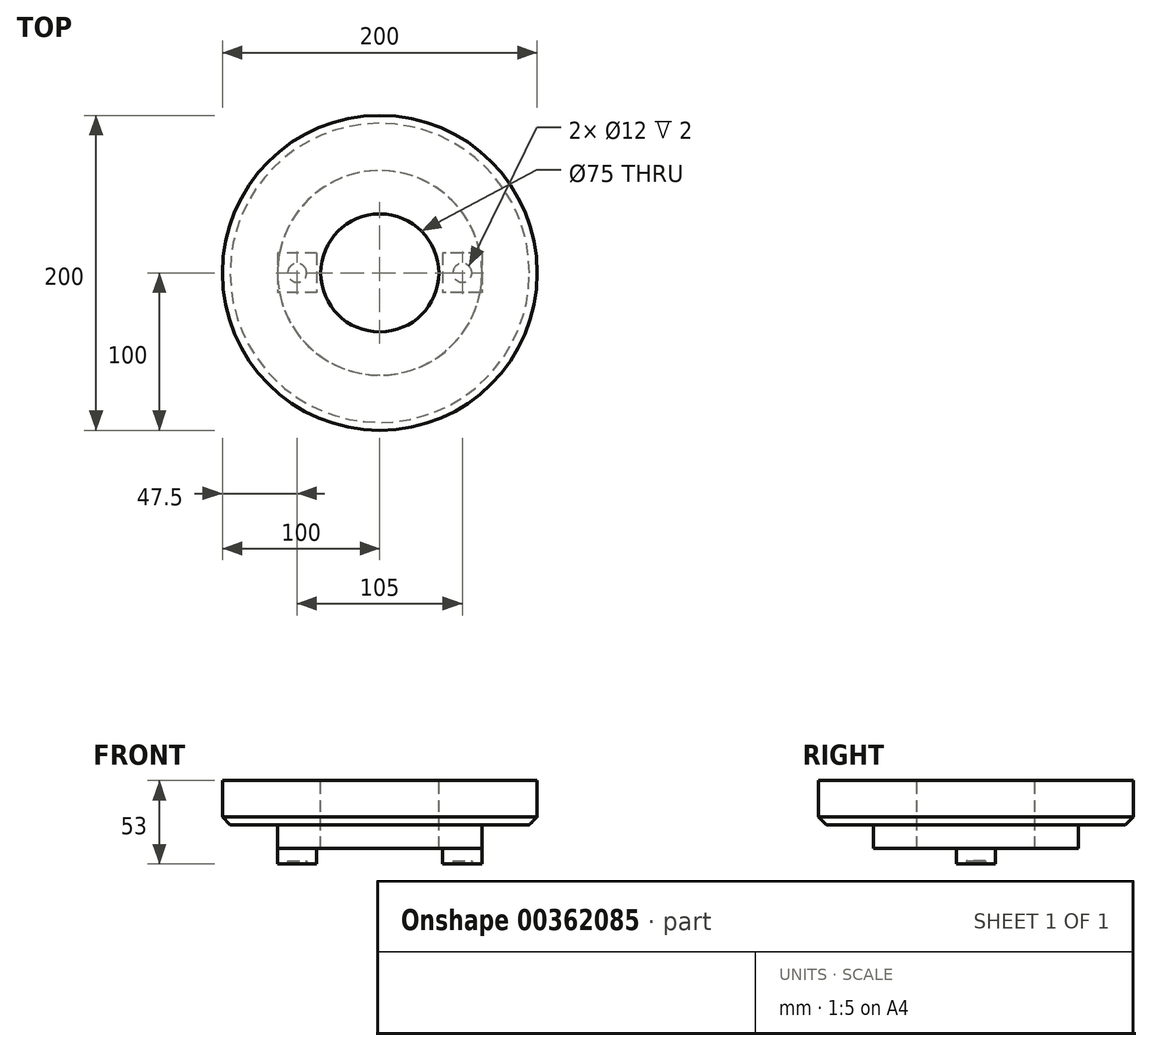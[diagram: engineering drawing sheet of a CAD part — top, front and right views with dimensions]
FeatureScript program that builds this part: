
annotation { "Feature Type Name" : "Feature", "Feature Type Description" : "" }
export const myFeature = defineFeature(function(context is Context, id is Id, definition is map)
    precondition{}
    {
        {
            var Q0;
            Q0=qCreatedBy(makeId("Top.planeOp"),FACE);
            var sketch = newSketch(context, id + "F0", { "sketchPlane" : qUnion([Q0])});
            skCircle(sketch, "E0", {"center": v(0, 0) * mm, "radius": 100 * mm});
            skSolve(sketch);
        }
        {
            var Q0;
            Q0=makeQuery(id+"F0.imprint","IMPRINT",FACE,{"disambiguationData":[TD([[makeQuery(id+"F0.imprint","IMPRINT",EDGE,{"derivedFrom":sQuery(id+"F0.wireOp",EDGE,"E0")}),1.0]])]});
            extrude(context, id + "F1", {"entities" : qUnion([Q0]), "depth" : 28 * mm});
        }
        {
            var Q0;
            Q0=makeQuery(id+"F1.opExtrude","CAP_FACE",FACE,{"disambiguationData":[OSD([sQuery(id+"F0.wireOp",EDGE,"E0")])],"isStart":true});
            var sketch = newSketch(context, id + "F2", { "sketchPlane" : qUnion([Q0])});
            skCircle(sketch, "E1", {"center": v(0, 0) * mm, "radius": 65 * mm});
            skCircle(sketch, "E2", {"center": v(0, 0) * mm, "radius": 37.5 * mm});
            skPoint(sketch, "E3.middle", {"position": v(-47.86, 0) * mm});
            skPoint(sketch, "E4.middle", {"position": v(50, 0) * mm});
            skPoint(sketch, "E3.right.end.orphan", {"position": v(-60.36, 12.5) * mm});
            skPoint(sketch, "E3.bottom.end.orphan", {"position": v(-60.36, -12.5) * mm});
            skPoint(sketch, "E3.left.end.orphan", {"position": v(-35.36, 12.5) * mm});
            skPoint(sketch, "E3.left.start.orphan", {"position": v(-35.36, -12.5) * mm});
            skPoint(sketch, "E4.bottom.end.orphan", {"position": v(36.21, -12.5) * mm});
            skPoint(sketch, "E4.left.start.orphan", {"position": v(63.79, -12.5) * mm});
            skPoint(sketch, "E4.top.end.orphan", {"position": v(36.21, 12.5) * mm});
            skPoint(sketch, "E4.top.start.orphan", {"position": v(63.79, 12.5) * mm});
            skSolve(sketch);
        }
        {
            var Q0;
            Q0=makeQuery(id+"F2.imprint","IMPRINT",FACE,{"disambiguationData":[TD([[makeQuery(id+"F2.imprint","IMPRINT",EDGE,{"derivedFrom":sQuery(id+"F2.wireOp",EDGE,"E1")}),1.0]])]});
            extrude(context, id + "F3", {"entities" : qUnion([Q0]), "operationType" : NewBodyOperationType.ADD, "depth" : 15 * mm});
        }
        {
            var Q0;
            Q0=makeQuery(id+"F3.opExtrude","CAP_FACE",FACE,{"disambiguationData":[OSD([sQuery(id+"F2.wireOp",EDGE,"E1"),sQuery(id+"F2.wireOp",EDGE,"E2")])],"isStart":false});
            var sketch = newSketch(context, id + "F4", { "sketchPlane" : qUnion([Q0])});
            skLineSegment(sketch, "E5.bottom", {"start": v(65, -12.5) * mm, "end": v(40, -12.5) * mm});
            skLineSegment(sketch, "E5.top", {"start": v(65, 12.5) * mm, "end": v(40, 12.5) * mm});
            skLineSegment(sketch, "E5.left", {"start": v(65, -12.5) * mm, "end": v(65, 12.5) * mm});
            skLineSegment(sketch, "E5.right", {"start": v(40, -12.5) * mm, "end": v(40, 12.5) * mm});
            skPoint(sketch, "E5.middle", {"position": v(52.5, 0) * mm});
            skLineSegment(sketch, "E6.bottom", {"start": v(-40, -12.5) * mm, "end": v(-65, -12.5) * mm});
            skLineSegment(sketch, "E6.top", {"start": v(-40, 12.5) * mm, "end": v(-65, 12.5) * mm});
            skLineSegment(sketch, "E6.left", {"start": v(-40, -12.5) * mm, "end": v(-40, 12.5) * mm});
            skLineSegment(sketch, "E6.right", {"start": v(-65, -12.5) * mm, "end": v(-65, 12.5) * mm});
            skPoint(sketch, "E6.middle", {"position": v(-52.5, 0) * mm});
            skSolve(sketch);
        }
        {
            var Q0;
            {var subQ0=sQuery(id+"F4.wireOp",EDGE,"E6.left");Q0=makeQuery(id+"F4.imprint","IMPRINT",FACE,{"disambiguationData":[TD([[makeQuery(id+"F4.imprint","IMPRINT",EDGE,{"derivedFrom":subQ0}),1.0]])]});}
            var Q1;
            {var subQ4=sQuery(id+"F4.wireOp",EDGE,"E5.right");Q1=makeQuery(id+"F4.imprint","IMPRINT",FACE,{"disambiguationData":[TD([[makeQuery(id+"F4.imprint","IMPRINT",EDGE,{"derivedFrom":subQ4}),-1.0]])]});}
            var Q2;
            {var subQ0=sQuery(id+"F4.wireOp",EDGE,"E5.left");var subQ1=sQuery(id+"F4.wireOp",EDGE,"E5.top");var subQ2=makeQuery(id+"F4.imprint","INTERSECT",VERTEX,{"derivedFrom":[subQ1,subQ0]});Q2=makeQuery(id+"F4.imprint","IMPRINT",FACE,{"disambiguationData":[TD([[makeQuery(id+"F4.imprint","IMPRINT",EDGE,{"disambiguationData":[TD([[subQ2,-1.0]])],"derivedFrom":subQ1}),1.0]])]});}
            var Q3;
            {var subQ0=sQuery(id+"F4.wireOp",EDGE,"E5.left");var subQ1=sQuery(id+"F4.wireOp",EDGE,"E5.bottom");var subQ2=makeQuery(id+"F4.imprint","INTERSECT",VERTEX,{"derivedFrom":[subQ1,subQ0]});Q3=makeQuery(id+"F4.imprint","IMPRINT",FACE,{"disambiguationData":[TD([[makeQuery(id+"F4.imprint","IMPRINT",EDGE,{"disambiguationData":[TD([[subQ2,-1.0]])],"derivedFrom":subQ1}),-1.0]])]});}
            var Q4;
            {var subQ0=sQuery(id+"F4.wireOp",EDGE,"E6.right");var subQ1=sQuery(id+"F4.wireOp",EDGE,"E6.top");var subQ2=makeQuery(id+"F4.imprint","INTERSECT",VERTEX,{"derivedFrom":[subQ1,subQ0]});Q4=makeQuery(id+"F4.imprint","IMPRINT",FACE,{"disambiguationData":[TD([[makeQuery(id+"F4.imprint","IMPRINT",EDGE,{"disambiguationData":[TD([[subQ2,1.0]])],"derivedFrom":subQ1}),1.0]])]});}
            var Q5;
            {var subQ0=sQuery(id+"F4.wireOp",EDGE,"E6.right");var subQ1=sQuery(id+"F4.wireOp",EDGE,"E6.bottom");var subQ2=makeQuery(id+"F4.imprint","INTERSECT",VERTEX,{"derivedFrom":[subQ1,subQ0]});Q5=makeQuery(id+"F4.imprint","IMPRINT",FACE,{"disambiguationData":[TD([[makeQuery(id+"F4.imprint","IMPRINT",EDGE,{"disambiguationData":[TD([[subQ2,1.0]])],"derivedFrom":subQ1}),-1.0]])]});}
            extrude(context, id + "F5", {"entities" : qUnion([Q0, Q1, Q2, Q3, Q4, Q5]), "operationType" : NewBodyOperationType.ADD, "depth" : 10 * mm});
        }
        {
            var Q0;
            Q0=makeQuery(id+"F5.opExtrude","CAP_FACE",FACE,{"disambiguationData":[OSD([sQuery(id+"F4.wireOp",EDGE,"E6.bottom"),sQuery(id+"F4.wireOp",EDGE,"E6.top"),sQuery(id+"F4.wireOp",EDGE,"E6.left"),sQuery(id+"F4.wireOp",EDGE,"E6.right")])],"isStart":false});
            var sketch = newSketch(context, id + "F6", { "sketchPlane" : qUnion([Q0])});
            skCircle(sketch, "E7", {"center": v(-52.5, 0) * mm, "radius": 6 * mm});
            skCircle(sketch, "E8", {"center": v(52.5, 0) * mm, "radius": 6 * mm});
            skSolve(sketch);
        }
        {
            var Q0;
            Q0=makeQuery(id+"F6.imprint","IMPRINT",FACE,{"disambiguationData":[TD([[makeQuery(id+"F6.imprint","IMPRINT",EDGE,{"derivedFrom":sQuery(id+"F6.wireOp",EDGE,"E8")}),1.0]])]});
            var Q1;
            Q1=makeQuery(id+"F6.imprint","IMPRINT",FACE,{"disambiguationData":[TD([[makeQuery(id+"F6.imprint","IMPRINT",EDGE,{"derivedFrom":sQuery(id+"F6.wireOp",EDGE,"E7")}),1.0]])]});
            extrude(context, id + "F7", {"entities" : qUnion([Q0, Q1]), "operationType" : NewBodyOperationType.REMOVE, "oppositeDirection" : true, "depth" : 2 * mm});
        }
        {
            var Q0;
            Q0=makeQuery(id+"F3.boolean.opBoolean","SPLIT",FACE,{"disambiguationData":[TD([makeQuery(id+"F3.opExtrude","SWEPT_FACE",FACE,{"disambiguationData":[OSD([sQuery(id+"F2.wireOp",EDGE,"E2")])]})])],"derivedFrom":makeQuery(id+"F1.opExtrude","CAP_FACE",FACE,{"disambiguationData":[OSD([sQuery(id+"F0.wireOp",EDGE,"E0")])],"isStart":true})});
            extrude(context, id + "F8", {"entities" : qUnion([Q0]), "operationType" : NewBodyOperationType.REMOVE, "oppositeDirection" : true, "depth" : 50 * mm});
        }
        {
            var Q0;
            Q0=makeQuery(id+"F1.opExtrude","CAP_EDGE",EDGE,{"disambiguationData":[OSD([sQuery(id+"F0.wireOp",EDGE,"E0")])],"isStart":true});
            chamfer(context, id + "F9", {"entities" : qUnion([Q0]), "width" : 5 * mm, "tangentPropagation" : true});
        }
    });
